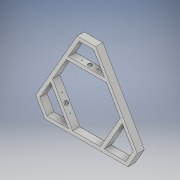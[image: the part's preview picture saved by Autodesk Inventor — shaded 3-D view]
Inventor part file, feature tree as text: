
AUTODESK INVENTOR PART (.ipt)
format: ipt  version: 2018 (Build 220112000, 112)  size: 228,864 bytes
history: native  units: in
note: dims shown in document units (in); Inventor stores cm internally (conversion verified against a paired STEP export)
features: extrude x5, sketch x5, shell x1
ambient origin geometry x8: Origin, YZ Plane, XZ Plane, XY Plane, X Axis, Y Axis, Z Axis, Center Point
bodies: Solid1 (feature_tree)
feature tree (11):
  extrude  "Extrusion1"  Depth=6.0in
  extrude  "Extrusion2"  Depth=6.0in
  extrude  "Extrusion3"  Depth=1.0in
  sketch  "Sketch4"  dims[d24=2.0in d25=0.0in d26=2.0in d27=0.0in]
  shell  "Shell1"  Thickness=1.1811in
  extrude  "Extrusion4"  Depth=2.0in TaperAngle=0.0deg
  extrude  "Extrusion5"  Depth=1.0in
  sketch  "Sketch1"  dims[d0=10.0in d1=6.0in]
  sketch  "Sketch2"  dims[d2=60.0deg d3=6.0in]
  sketch  "Sketch3"  dims[d4=60.0deg d11=1.0in d20=1.1811in d22=360.0deg]
  sketch  "Sketch5"  dims[d28=2.0in d29=0.0in d30=1.0in d31=90.0deg d32=1.125in d33=0.0625in d34=2.25in d35=2.25in d36=0.196in d37=0.196in d38=1.0in d39=0.0in d40=1.0in d41=180.0deg d42=2.25in d43=2.25in d44=0.196in d45=0.196in d46=1.125in d47=1.0in d48=0.0in]
